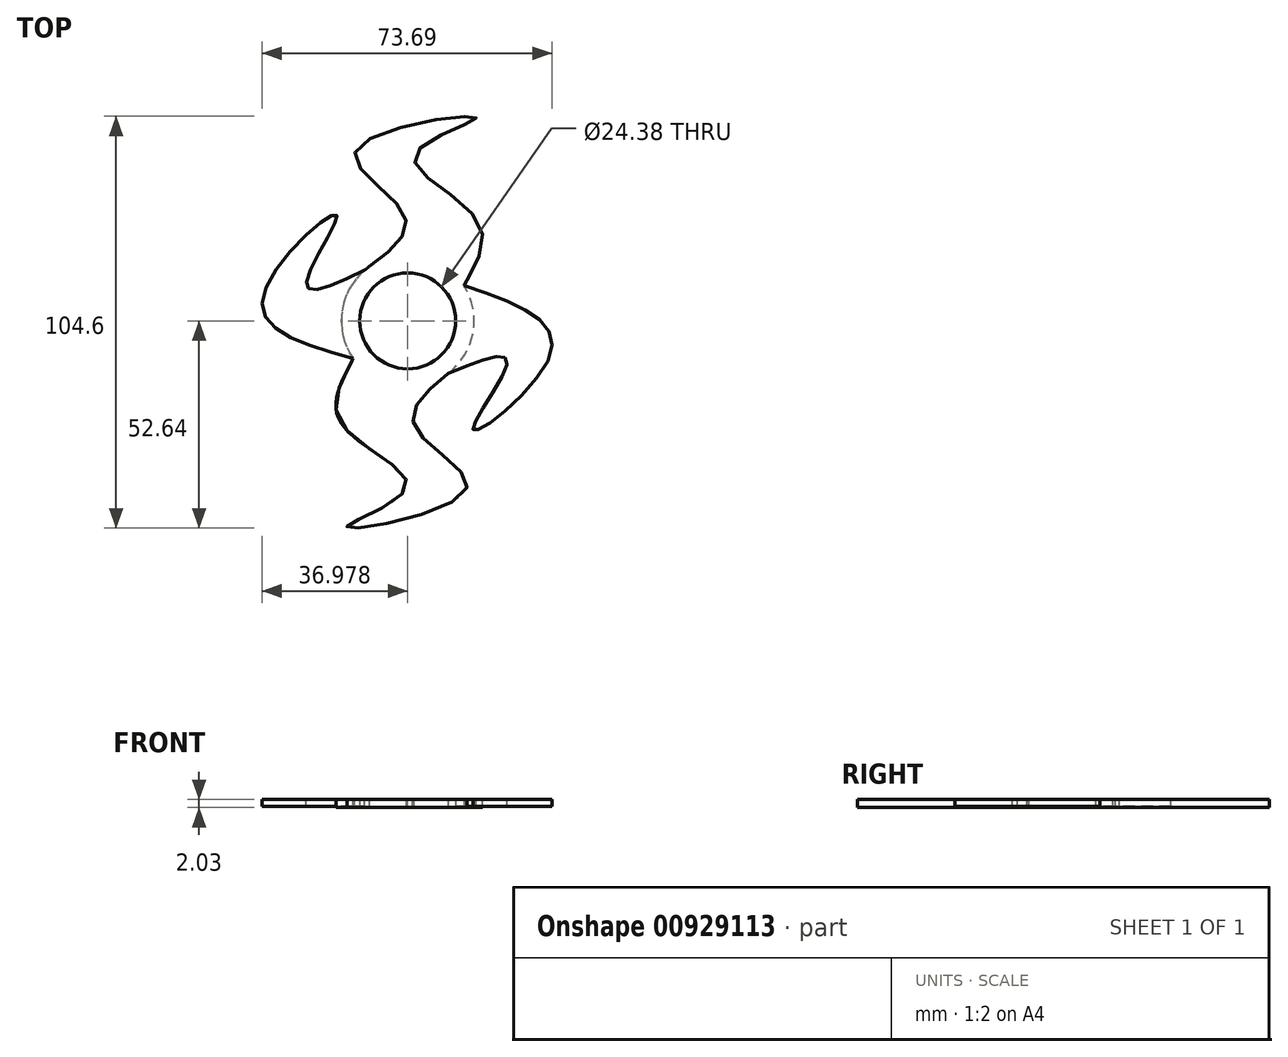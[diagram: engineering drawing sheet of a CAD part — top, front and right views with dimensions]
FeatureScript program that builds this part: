
annotation { "Feature Type Name" : "Feature", "Feature Type Description" : "" }
export const myFeature = defineFeature(function(context is Context, id is Id, definition is map)
    precondition{}
    {
        {
            var Q0;
            Q0=qCreatedBy(makeId("Top.planeOp"),FACE);
            var sketch = newSketch(context, id + "F0", { "sketchPlane" : qUnion([Q0])});
            skCircle(sketch, "E0", {"center": v(3.52, 24.43) * mm, "radius": 16.87 * mm});
            skCircle(sketch, "E1", {"center": v(3.52, 24.43) * mm, "radius": 12.19 * mm});
            skFitSpline(sketch, "E2", {"points": [v(-6.28, 38.16) * mm, v(2.68, 51.44) * mm, v(-9.63, 67.88) * mm, v(20.92, 76.08) * mm, v(5.3, 66.48) * mm, v(22.15, 48.05) * mm, v(17.82, 33.38) * mm, v(18.15, 32.81) * mm], "startDerivative": vector(117.85, 89.26) * mm, "endDerivative": vector(20.87, -11.19) * mm});
            skFitSpline(sketch, "E3", {"points": [v(13.78, 11.05) * mm, v(5.38, -2.65) * mm, v(18.3, -18.62) * mm, v(-11.92, -27.96) * mm, v(3.32, -17.78) * mm, v(-14.21, 0) * mm, v(-10.43, 14.83) * mm, v(-10.79, 15.38) * mm], "startDerivative": vector(-114.4, -93.64) * mm, "endDerivative": vector(-21.28, 10.4) * mm});
            skSolve(sketch);
        }
        {
            var Q0;
            Q0 = qSketchRegion(id + "F0", true);
            extrude(context, id + "F1", {"entities" : qUnion([Q0]), "depth" : 2.03 * mm, "offsetDistance" : 25.4 * mm});
        }
        {
            var Q0;
            Q0=makeQuery(id+"F1.opExtrude","CAP_FACE",FACE,{"disambiguationData":[OSD([sQuery(id+"F0.wireOp",EDGE,"E0"),sQuery(id+"F0.wireOp",EDGE,"E1"),sQuery(id+"F0.wireOp",EDGE,"E2"),sQuery(id+"F0.wireOp",EDGE,"E3")])],"isStart":false});
            var sketch = newSketch(context, id + "F2", { "sketchPlane" : qUnion([Q0])});
            skFitSpline(sketch, "E4", {"points": [v(17.82, 33.38) * mm, v(40, 16.67) * mm, v(20.15, -3.26) * mm, v(28.76, 13.92) * mm, v(13.78, 11.05) * mm], "startDerivative": vector(130.4, -43.66) * mm, "endDerivative": vector(-108.77, -45.02) * mm});
            skFitSpline(sketch, "E5", {"points": [v(-10.3, 14.85) * mm, v(-33.31, 30.38) * mm, v(-14.53, 51.32) * mm, v(-22.24, 33.7) * mm, v(-7.38, 37.3) * mm], "startDerivative": vector(-132.5, 36.8) * mm, "endDerivative": vector(106.27, 50.63) * mm});
            skSolve(sketch);
        }
        {
            var Q0;
            {var subQ0=sQuery(id+"F2.wireOp",EDGE,"E5");var subQ1=sQuery(id+"F0.wireOp",EDGE,"E3");var subQ6=makeQuery(id+"F1.opExtrude","CAP_EDGE",EDGE,{"disambiguationData":[OSD([subQ1])],"isStart":false});var subQ7=makeQuery(id+"F2.imprint","INTERSECT",VERTEX,{"derivedFrom":[subQ6,subQ0]});Q0=makeQuery(id+"F2.imprint","IMPRINT",FACE,{"disambiguationData":[TD([[makeQuery(id+"F2.imprint","IMPRINT",EDGE,{"disambiguationData":[TD([[subQ7,-1.0]])],"derivedFrom":subQ0}),-1.0]])]});}
            extrude(context, id + "F3", {"entities" : qUnion([Q0]), "operationType" : NewBodyOperationType.ADD, "oppositeDirection" : true, "depth" : 1.78 * mm, "offsetDistance" : 25.4 * mm});
        }
        {
            var Q0;
            Q0=makeQuery(id+"F2.imprint","IMPRINT",FACE,{"disambiguationData":[TD([[makeQuery(id+"F2.imprint","IMPRINT",EDGE,{"derivedFrom":sQuery(id+"F2.wireOp",EDGE,"E4")}),-1.0]])]});
            extrude(context, id + "F4", {"entities" : qUnion([Q0]), "operationType" : NewBodyOperationType.ADD, "oppositeDirection" : true, "depth" : 1.78 * mm, "offsetDistance" : 25.4 * mm});
        }
    });
